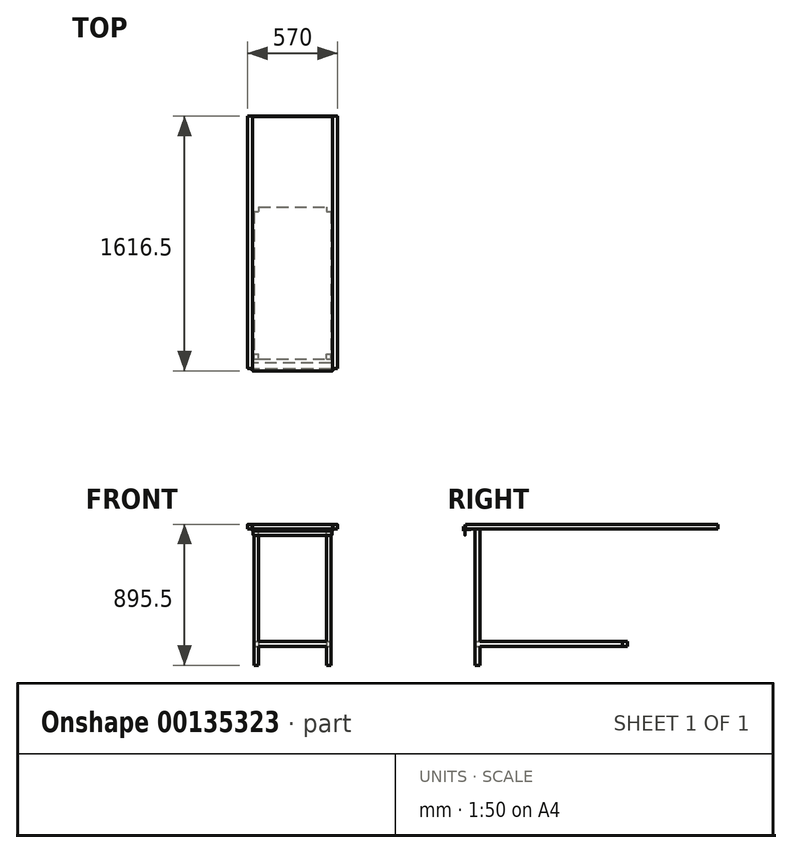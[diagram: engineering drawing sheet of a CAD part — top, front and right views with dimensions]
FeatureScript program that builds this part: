
annotation { "Feature Type Name" : "Feature", "Feature Type Description" : "" }
export const myFeature = defineFeature(function(context is Context, id is Id, definition is map)
    precondition{}
    {
        {
            var Q0;
            Q0=qCreatedBy(makeId("Front.planeOp"),FACE);
            var sketch = newSketch(context, id + "F0", { "sketchPlane" : qUnion([Q0])});
            skLineSegment(sketch, "E0", {"start": v(-285, 0) * mm, "end": v(-285, 28.5) * mm});
            skLineSegment(sketch, "E1", {"start": v(-283.5, 30) * mm, "end": v(-256.5, 30) * mm});
            skLineSegment(sketch, "E2", {"start": v(-255, 28.5) * mm, "end": v(-255, 3) * mm});
            skLineSegment(sketch, "E3", {"start": v(-253.5, 1.5) * mm, "end": v(253.5, 1.5) * mm});
            skLineSegment(sketch, "E4", {"start": v(255, 3) * mm, "end": v(255, 28.5) * mm});
            skLineSegment(sketch, "E5", {"start": v(256.5, 30) * mm, "end": v(283.5, 30) * mm});
            skLineSegment(sketch, "E6", {"start": v(285, 28.5) * mm, "end": v(285, 0) * mm});
            skPoint(sketch, "E7.visualSharp", {"position": v(-285, 30) * mm});
            skArc(sketch, "E7.filletArc", {"start": v(-283.5, 30) * mm, "mid": v(-284.56, 29.56) * mm, "end": v(-285, 28.5) * mm});
            skPoint(sketch, "E8.visualSharp", {"position": v(-255, 30) * mm});
            skArc(sketch, "E8.filletArc", {"start": v(-255, 28.5) * mm, "mid": v(-255.44, 29.56) * mm, "end": v(-256.5, 30) * mm});
            skPoint(sketch, "E9.visualSharp", {"position": v(-255, 1.5) * mm});
            skArc(sketch, "E9.filletArc", {"start": v(-255, 3) * mm, "mid": v(-254.56, 1.94) * mm, "end": v(-253.5, 1.5) * mm});
            skPoint(sketch, "E10.visualSharp", {"position": v(255, 1.5) * mm});
            skArc(sketch, "E10.filletArc", {"start": v(253.5, 1.5) * mm, "mid": v(254.56, 1.94) * mm, "end": v(255, 3) * mm});
            skPoint(sketch, "E11.visualSharp", {"position": v(255, 30) * mm});
            skArc(sketch, "E11.filletArc", {"start": v(256.5, 30) * mm, "mid": v(255.44, 29.56) * mm, "end": v(255, 28.5) * mm});
            skPoint(sketch, "E12.visualSharp", {"position": v(285, 30) * mm});
            skArc(sketch, "E12.filletArc", {"start": v(285, 28.5) * mm, "mid": v(284.56, 29.56) * mm, "end": v(283.5, 30) * mm});
            skLineSegment(sketch, "E13.0", {"start": v(283.5, 28.5) * mm, "end": v(283.5, 0) * mm});
            skLineSegment(sketch, "E13.1", {"start": v(256.5, 28.5) * mm, "end": v(283.5, 28.5) * mm});
            skLineSegment(sketch, "E13.2", {"start": v(256.5, 3) * mm, "end": v(256.5, 28.5) * mm});
            skArc(sketch, "E13.3", {"start": v(253.5, 0) * mm, "mid": v(255.62, 0.88) * mm, "end": v(256.5, 3) * mm});
            skLineSegment(sketch, "E13.4", {"start": v(-253.5, 0) * mm, "end": v(253.5, 0) * mm});
            skLineSegment(sketch, "E13.5", {"start": v(-283.5, 0) * mm, "end": v(-283.5, 28.5) * mm});
            skLineSegment(sketch, "E13.6", {"start": v(-283.5, 28.5) * mm, "end": v(-256.5, 28.5) * mm});
            skLineSegment(sketch, "E13.7", {"start": v(-256.5, 28.5) * mm, "end": v(-256.5, 3) * mm});
            skArc(sketch, "E13.8", {"start": v(-256.5, 3) * mm, "mid": v(-255.62, 0.88) * mm, "end": v(-253.5, 0) * mm});
            skLineSegment(sketch, "E14", {"start": v(-285, 0) * mm, "end": v(-283.5, 0) * mm});
            skLineSegment(sketch, "E15", {"start": v(283.5, 0) * mm, "end": v(285, 0) * mm});
            skSolve(sketch);
        }
        {
            var Q0;
            Q0 = qSketchRegion(id + "F0", true);
            extrude(context, id + "F1", {"entities" : qUnion([Q0]), "depth" : 1600 * mm, "offsetDistance" : 25 * mm});
        }
        {
            var Q0;
            Q0=makeQuery(id+"F1.opExtrude","CAP_FACE",FACE,{"disambiguationData":[OSD([sQuery(id+"F0.wireOp",EDGE,"E0"),sQuery(id+"F0.wireOp",EDGE,"E1"),sQuery(id+"F0.wireOp",EDGE,"E2"),sQuery(id+"F0.wireOp",EDGE,"E3"),sQuery(id+"F0.wireOp",EDGE,"E4"),sQuery(id+"F0.wireOp",EDGE,"E5"),sQuery(id+"F0.wireOp",EDGE,"E6"),sQuery(id+"F0.wireOp",EDGE,"E7.filletArc"),sQuery(id+"F0.wireOp",EDGE,"E8.filletArc"),sQuery(id+"F0.wireOp",EDGE,"E9.filletArc"),sQuery(id+"F0.wireOp",EDGE,"E10.filletArc"),sQuery(id+"F0.wireOp",EDGE,"E11.filletArc"),sQuery(id+"F0.wireOp",EDGE,"E12.filletArc"),sQuery(id+"F0.wireOp",EDGE,"E13.0"),sQuery(id+"F0.wireOp",EDGE,"E13.1"),sQuery(id+"F0.wireOp",EDGE,"E13.2"),sQuery(id+"F0.wireOp",EDGE,"E13.3"),sQuery(id+"F0.wireOp",EDGE,"E13.4"),sQuery(id+"F0.wireOp",EDGE,"E13.5"),sQuery(id+"F0.wireOp",EDGE,"E13.6"),sQuery(id+"F0.wireOp",EDGE,"E13.7"),sQuery(id+"F0.wireOp",EDGE,"E13.8"),sQuery(id+"F0.wireOp",EDGE,"E14"),sQuery(id+"F0.wireOp",EDGE,"E15")])],"isStart":true});
            var sketch = newSketch(context, id + "F2", { "sketchPlane" : qUnion([Q0])});
            skLineSegment(sketch, "E16.0", {"start": v(-285, 28.5) * mm, "end": v(-285, 0) * mm});
            skArc(sketch, "E16.3", {"start": v(283.5, 30) * mm, "mid": v(284.56, 29.56) * mm, "end": v(285, 28.5) * mm});
            skLineSegment(sketch, "E16.4", {"start": v(285, 0) * mm, "end": v(285, 28.5) * mm});
            skArc(sketch, "E16.10", {"start": v(-285, 28.5) * mm, "mid": v(-284.56, 29.56) * mm, "end": v(-283.5, 30) * mm});
            skLineSegment(sketch, "E17", {"start": v(285, 0) * mm, "end": v(-285, 0) * mm});
            skLineSegment(sketch, "E18", {"start": v(-283.5, 30) * mm, "end": v(283.5, 30) * mm});
            skSolve(sketch);
        }
        {
            var Q0;
            Q0 = qSketchRegion(id + "F2", true);
            extrude(context, id + "F3", {"entities" : qUnion([Q0]), "operationType" : NewBodyOperationType.ADD, "depth" : 1.5 * mm});
        }
        {
            var Q0;
            Q0=makeQuery(id+"F1.opExtrude","CAP_FACE",FACE,{"disambiguationData":[OSD([sQuery(id+"F0.wireOp",EDGE,"E0"),sQuery(id+"F0.wireOp",EDGE,"E1"),sQuery(id+"F0.wireOp",EDGE,"E2"),sQuery(id+"F0.wireOp",EDGE,"E3"),sQuery(id+"F0.wireOp",EDGE,"E4"),sQuery(id+"F0.wireOp",EDGE,"E5"),sQuery(id+"F0.wireOp",EDGE,"E6"),sQuery(id+"F0.wireOp",EDGE,"E7.filletArc"),sQuery(id+"F0.wireOp",EDGE,"E8.filletArc"),sQuery(id+"F0.wireOp",EDGE,"E9.filletArc"),sQuery(id+"F0.wireOp",EDGE,"E10.filletArc"),sQuery(id+"F0.wireOp",EDGE,"E11.filletArc"),sQuery(id+"F0.wireOp",EDGE,"E12.filletArc"),sQuery(id+"F0.wireOp",EDGE,"E13.0"),sQuery(id+"F0.wireOp",EDGE,"E13.1"),sQuery(id+"F0.wireOp",EDGE,"E13.2"),sQuery(id+"F0.wireOp",EDGE,"E13.3"),sQuery(id+"F0.wireOp",EDGE,"E13.4"),sQuery(id+"F0.wireOp",EDGE,"E13.5"),sQuery(id+"F0.wireOp",EDGE,"E13.6"),sQuery(id+"F0.wireOp",EDGE,"E13.7"),sQuery(id+"F0.wireOp",EDGE,"E13.8"),sQuery(id+"F0.wireOp",EDGE,"E14"),sQuery(id+"F0.wireOp",EDGE,"E15")])],"isStart":false});
            var sketch = newSketch(context, id + "F4", { "sketchPlane" : qUnion([Q0])});
            skLineSegment(sketch, "E19.0", {"start": v(256.5, 3) * mm, "end": v(256.5, 15) * mm});
            skLineSegment(sketch, "E19.1", {"start": v(-256.5, 15) * mm, "end": v(-256.5, 3) * mm});
            skArc(sketch, "E19.2", {"start": v(-256.5, 3) * mm, "mid": v(-255.62, 0.88) * mm, "end": v(-253.5, 0) * mm});
            skLineSegment(sketch, "E19.3", {"start": v(-253.5, 0) * mm, "end": v(253.5, 0) * mm});
            skArc(sketch, "E19.4", {"start": v(253.5, 0) * mm, "mid": v(255.62, 0.88) * mm, "end": v(256.5, 3) * mm});
            skLineSegment(sketch, "E20.0", {"start": v(255, 3) * mm, "end": v(255, 15) * mm});
            skLineSegment(sketch, "E20.1", {"start": v(-255, 15) * mm, "end": v(-255, 3) * mm});
            skArc(sketch, "E20.2", {"start": v(-255, 3) * mm, "mid": v(-254.56, 1.94) * mm, "end": v(-253.5, 1.5) * mm});
            skLineSegment(sketch, "E20.3", {"start": v(-253.5, 1.5) * mm, "end": v(253.5, 1.5) * mm});
            skArc(sketch, "E20.4", {"start": v(253.5, 1.5) * mm, "mid": v(254.56, 1.94) * mm, "end": v(255, 3) * mm});
            skLineSegment(sketch, "E21", {"start": v(-256.5, 15) * mm, "end": v(-255, 15) * mm});
            skLineSegment(sketch, "E22", {"start": v(255, 15) * mm, "end": v(256.5, 15) * mm});
            skSolve(sketch);
        }
        {
            var Q0;
            Q0 = qSketchRegion(id + "F4", true);
            extrude(context, id + "F5", {"entities" : qUnion([Q0]), "operationType" : NewBodyOperationType.ADD, "depth" : 13.5 * mm});
        }
        {
            var Q0;
            Q0=makeQuery(id+"F5.opExtrude","CAP_FACE",FACE,{"disambiguationData":[OSD([sQuery(id+"F4.wireOp",EDGE,"E19.0"),sQuery(id+"F4.wireOp",EDGE,"E19.1"),sQuery(id+"F4.wireOp",EDGE,"E19.2"),sQuery(id+"F4.wireOp",EDGE,"E19.3"),sQuery(id+"F4.wireOp",EDGE,"E19.4"),sQuery(id+"F4.wireOp",EDGE,"E20.0"),sQuery(id+"F4.wireOp",EDGE,"E20.1"),sQuery(id+"F4.wireOp",EDGE,"E20.2"),sQuery(id+"F4.wireOp",EDGE,"E20.3"),sQuery(id+"F4.wireOp",EDGE,"E20.4"),sQuery(id+"F4.wireOp",EDGE,"E21"),sQuery(id+"F4.wireOp",EDGE,"E22")])],"isStart":false});
            var sketch = newSketch(context, id + "F6", { "sketchPlane" : qUnion([Q0])});
            skLineSegment(sketch, "E23.bottom", {"start": v(-253.5, 1.5) * mm, "end": v(253.5, 1.5) * mm});
            skLineSegment(sketch, "E23.top", {"start": v(-253.5, 0) * mm, "end": v(253.5, 0) * mm});
            skLineSegment(sketch, "E23.left", {"start": v(-253.5, 1.5) * mm, "end": v(-253.5, 0) * mm});
            skLineSegment(sketch, "E23.right", {"start": v(253.5, 1.5) * mm, "end": v(253.5, 0) * mm});
            skSolve(sketch);
        }
        {
            var Q0;
            Q0 = qSketchRegion(id + "F6", true);
            var Q1;
            Q1=sQuery(id+"F6.wireOp",EDGE,"E23.top");
            revolve(context, id + "F7", {"operationType" : NewBodyOperationType.ADD, "entities" : qUnion([Q0]), "axis" : qUnion([Q1]), "revolveType" : RevolveType.ONE_DIRECTION, "angle" : 90 * degree});
        }
        {
            var Q0;
            Q0=makeQuery(id+"F7.boolean.opBoolean","MERGE",FACE,{"derivedFrom":[makeQuery(id+"F5.boolean.opBoolean","MERGE",FACE,{"derivedFrom":[makeQuery(id+"F3.boolean.opBoolean","MERGE",FACE,{"derivedFrom":[makeQuery(id+"F1.opExtrude","SWEPT_FACE",FACE,{"disambiguationData":[OSD([sQuery(id+"F0.wireOp",EDGE,"E13.4")])]}),makeQuery(id+"F1.opExtrude","SWEPT_FACE",FACE,{"disambiguationData":[OSD([sQuery(id+"F0.wireOp",EDGE,"E14")])]}),makeQuery(id+"F1.opExtrude","SWEPT_FACE",FACE,{"disambiguationData":[OSD([sQuery(id+"F0.wireOp",EDGE,"E15")])]}),makeQuery(id+"F3.opExtrude","SWEPT_FACE",FACE,{"disambiguationData":[OSD([sQuery(id+"F2.wireOp",EDGE,"E17")])]})]}),makeQuery(id+"F5.opExtrude","SWEPT_FACE",FACE,{"disambiguationData":[OSD([sQuery(id+"F4.wireOp",EDGE,"E19.3")])]})]}),makeQuery(id+"F7.opRevolve","CAP_FACE",FACE,{"disambiguationData":[OSD([sQuery(id+"F6.wireOp",EDGE,"E23.bottom"),sQuery(id+"F6.wireOp",EDGE,"E23.top"),sQuery(id+"F6.wireOp",EDGE,"E23.left"),sQuery(id+"F6.wireOp",EDGE,"E23.right")])],"isStart":false})]});
            var sketch = newSketch(context, id + "F8", { "sketchPlane" : qUnion([Q0])});
            skLineSegment(sketch, "E24.bottom", {"start": v(-253.5, 1615) * mm, "end": v(253.5, 1615) * mm});
            skLineSegment(sketch, "E24.top", {"start": v(-253.5, 1613.5) * mm, "end": v(253.5, 1613.5) * mm});
            skLineSegment(sketch, "E24.left", {"start": v(-253.5, 1615) * mm, "end": v(-253.5, 1613.5) * mm});
            skLineSegment(sketch, "E24.right", {"start": v(253.5, 1615) * mm, "end": v(253.5, 1613.5) * mm});
            skSolve(sketch);
        }
        {
            var Q0;
            Q0 = qSketchRegion(id + "F8", true);
            extrude(context, id + "F9", {"entities" : qUnion([Q0]), "operationType" : NewBodyOperationType.ADD, "depth" : 13.5 * mm});
        }
        {
            var Q0;
            Q0=makeQuery(id+"F1.opExtrude","SWEPT_FACE",FACE,{"disambiguationData":[OSD([sQuery(id+"F0.wireOp",EDGE,"E13.0")])]});
            var sketch = newSketch(context, id + "F10", { "sketchPlane" : qUnion([Q0])});
            skLineSegment(sketch, "E25.bottom", {"start": v(1600, 28.5) * mm, "end": v(1598.5, 28.5) * mm});
            skLineSegment(sketch, "E25.top", {"start": v(1600, 0) * mm, "end": v(1598.5, 0) * mm});
            skLineSegment(sketch, "E25.left", {"start": v(1600, 28.5) * mm, "end": v(1600, 0) * mm});
            skLineSegment(sketch, "E25.right", {"start": v(1598.5, 28.5) * mm, "end": v(1598.5, 0) * mm});
            skSolve(sketch);
        }
        {
            var Q0;
            Q0 = qSketchRegion(id + "F10", true);
            extrude(context, id + "F11", {"entities" : qUnion([Q0]), "operationType" : NewBodyOperationType.ADD, "endBound" : BoundingType.UP_TO_NEXT, "depth" : 25 * mm});
        }
        {
            var Q0;
            Q0=makeQuery(id+"F1.opExtrude","SWEPT_FACE",FACE,{"disambiguationData":[OSD([sQuery(id+"F0.wireOp",EDGE,"E13.5")])]});
            var sketch = newSketch(context, id + "F12", { "sketchPlane" : qUnion([Q0])});
            skLineSegment(sketch, "E26.bottom", {"start": v(-1600, 28.5) * mm, "end": v(-1598.5, 28.5) * mm});
            skLineSegment(sketch, "E26.top", {"start": v(-1600, 0) * mm, "end": v(-1598.5, 0) * mm});
            skLineSegment(sketch, "E26.left", {"start": v(-1600, 28.5) * mm, "end": v(-1600, 0) * mm});
            skLineSegment(sketch, "E26.right", {"start": v(-1598.5, 28.5) * mm, "end": v(-1598.5, 0) * mm});
            skSolve(sketch);
        }
        {
            var Q0;
            Q0 = qSketchRegion(id + "F12", true);
            extrude(context, id + "F13", {"entities" : qUnion([Q0]), "operationType" : NewBodyOperationType.ADD, "endBound" : BoundingType.UP_TO_NEXT, "depth" : 25 * mm});
        }
        {
            var Q0;
            Q0=makeQuery(id+"F13.boolean.opBoolean","MERGE",FACE,{"derivedFrom":[makeQuery(id+"F11.boolean.opBoolean","MERGE",FACE,{"derivedFrom":[makeQuery(id+"F7.boolean.opBoolean","MERGE",FACE,{"derivedFrom":[makeQuery(id+"F5.boolean.opBoolean","MERGE",FACE,{"derivedFrom":[makeQuery(id+"F3.boolean.opBoolean","MERGE",FACE,{"derivedFrom":[makeQuery(id+"F1.opExtrude","SWEPT_FACE",FACE,{"disambiguationData":[OSD([sQuery(id+"F0.wireOp",EDGE,"E13.4")])]}),makeQuery(id+"F1.opExtrude","SWEPT_FACE",FACE,{"disambiguationData":[OSD([sQuery(id+"F0.wireOp",EDGE,"E14")])]}),makeQuery(id+"F1.opExtrude","SWEPT_FACE",FACE,{"disambiguationData":[OSD([sQuery(id+"F0.wireOp",EDGE,"E15")])]}),makeQuery(id+"F3.opExtrude","SWEPT_FACE",FACE,{"disambiguationData":[OSD([sQuery(id+"F2.wireOp",EDGE,"E17")])]})]}),makeQuery(id+"F5.opExtrude","SWEPT_FACE",FACE,{"disambiguationData":[OSD([sQuery(id+"F4.wireOp",EDGE,"E19.3")])]})]}),makeQuery(id+"F7.opRevolve","CAP_FACE",FACE,{"disambiguationData":[OSD([sQuery(id+"F6.wireOp",EDGE,"E23.bottom"),sQuery(id+"F6.wireOp",EDGE,"E23.top"),sQuery(id+"F6.wireOp",EDGE,"E23.left"),sQuery(id+"F6.wireOp",EDGE,"E23.right")])],"isStart":false})]}),makeQuery(id+"F11.opExtrude","SWEPT_FACE",FACE,{"disambiguationData":[OSD([sQuery(id+"F10.wireOp",EDGE,"E25.top")])]})]}),makeQuery(id+"F13.opExtrude","SWEPT_FACE",FACE,{"disambiguationData":[OSD([sQuery(id+"F12.wireOp",EDGE,"E26.top")])]})]});
            var sketch = newSketch(context, id + "F14", { "sketchPlane" : qUnion([Q0])});
            skLineSegment(sketch, "E27.bottom", {"start": v(250, 1605.5) * mm, "end": v(-250, 1605.5) * mm});
            skLineSegment(sketch, "E27.top", {"start": v(245, 1565.5) * mm, "end": v(-245, 1565.5) * mm});
            skLineSegment(sketch, "E27.left", {"start": v(250, 1605.5) * mm, "end": v(250, 1570.5) * mm});
            skLineSegment(sketch, "E27.right", {"start": v(-250, 1605.5) * mm, "end": v(-250, 1570.5) * mm});
            skPoint(sketch, "E28.visualSharp", {"position": v(250, 1565.5) * mm});
            skArc(sketch, "E28.filletArc", {"start": v(245, 1565.5) * mm, "mid": v(248.54, 1566.96) * mm, "end": v(250, 1570.5) * mm});
            skPoint(sketch, "E29.visualSharp", {"position": v(-250, 1565.5) * mm});
            skArc(sketch, "E29.filletArc", {"start": v(-250, 1570.5) * mm, "mid": v(-248.54, 1566.96) * mm, "end": v(-245, 1565.5) * mm});
            skSolve(sketch);
        }
        {
            var Q0;
            Q0 = qSketchRegion(id + "F14", true);
            extrude(context, id + "F15", {"entities" : qUnion([Q0]), "operationType" : NewBodyOperationType.ADD, "depth" : 1.5 * mm});
        }
        {
            var Q0;
            Q0=makeQuery(id+"F15.opExtrude","CAP_FACE",FACE,{"disambiguationData":[OSD([sQuery(id+"F14.wireOp",EDGE,"E27.bottom"),sQuery(id+"F14.wireOp",EDGE,"E27.top"),sQuery(id+"F14.wireOp",EDGE,"E27.left"),sQuery(id+"F14.wireOp",EDGE,"E27.right"),sQuery(id+"F14.wireOp",EDGE,"E28.filletArc"),sQuery(id+"F14.wireOp",EDGE,"E29.filletArc")])],"isStart":false});
            var sketch = newSketch(context, id + "F16", { "sketchPlane" : qUnion([Q0])});
            skLineSegment(sketch, "E30.bottom", {"start": v(250, 1605.5) * mm, "end": v(-250, 1605.5) * mm});
            skLineSegment(sketch, "E30.top", {"start": v(250, 1604) * mm, "end": v(-250, 1604) * mm});
            skLineSegment(sketch, "E30.left", {"start": v(250, 1605.5) * mm, "end": v(250, 1604) * mm});
            skLineSegment(sketch, "E30.right", {"start": v(-250, 1605.5) * mm, "end": v(-250, 1604) * mm});
            skSolve(sketch);
        }
        {
            var Q0;
            Q0 = qSketchRegion(id + "F16", true);
            extrude(context, id + "F17", {"entities" : qUnion([Q0]), "operationType" : NewBodyOperationType.ADD, "depth" : 38.5 * mm});
        }
        {
            var Q0;
            Q0=makeQuery(id+"F17.opExtrude","CAP_EDGE",EDGE,{"disambiguationData":[OSD([sQuery(id+"F16.wireOp",EDGE,"E30.right")])],"isStart":false});
            var Q1;
            Q1=makeQuery(id+"F17.opExtrude","CAP_EDGE",EDGE,{"disambiguationData":[OSD([sQuery(id+"F16.wireOp",EDGE,"E30.left")])],"isStart":false});
            fillet(context, id + "F18", {"entities" : qUnion([Q0, Q1]), "radius" : 5 * mm, "tangentPropagation" : true, "allowEdgeOverflow" : false});
        }
        {
            var Q0;
            Q0=makeQuery(id+"F13.boolean.opBoolean","MERGE",FACE,{"derivedFrom":[makeQuery(id+"F11.boolean.opBoolean","MERGE",FACE,{"derivedFrom":[makeQuery(id+"F7.boolean.opBoolean","MERGE",FACE,{"derivedFrom":[makeQuery(id+"F5.boolean.opBoolean","MERGE",FACE,{"derivedFrom":[makeQuery(id+"F3.boolean.opBoolean","MERGE",FACE,{"derivedFrom":[makeQuery(id+"F1.opExtrude","SWEPT_FACE",FACE,{"disambiguationData":[OSD([sQuery(id+"F0.wireOp",EDGE,"E13.4")])]}),makeQuery(id+"F1.opExtrude","SWEPT_FACE",FACE,{"disambiguationData":[OSD([sQuery(id+"F0.wireOp",EDGE,"E14")])]}),makeQuery(id+"F1.opExtrude","SWEPT_FACE",FACE,{"disambiguationData":[OSD([sQuery(id+"F0.wireOp",EDGE,"E15")])]}),makeQuery(id+"F3.opExtrude","SWEPT_FACE",FACE,{"disambiguationData":[OSD([sQuery(id+"F2.wireOp",EDGE,"E17")])]})]}),makeQuery(id+"F5.opExtrude","SWEPT_FACE",FACE,{"disambiguationData":[OSD([sQuery(id+"F4.wireOp",EDGE,"E19.3")])]})]}),makeQuery(id+"F7.opRevolve","CAP_FACE",FACE,{"disambiguationData":[OSD([sQuery(id+"F6.wireOp",EDGE,"E23.bottom"),sQuery(id+"F6.wireOp",EDGE,"E23.top"),sQuery(id+"F6.wireOp",EDGE,"E23.left"),sQuery(id+"F6.wireOp",EDGE,"E23.right")])],"isStart":false})]}),makeQuery(id+"F11.opExtrude","SWEPT_FACE",FACE,{"disambiguationData":[OSD([sQuery(id+"F10.wireOp",EDGE,"E25.top")])]})]}),makeQuery(id+"F13.opExtrude","SWEPT_FACE",FACE,{"disambiguationData":[OSD([sQuery(id+"F12.wireOp",EDGE,"E26.top")])]})]});
            var sketch = newSketch(context, id + "F19", { "sketchPlane" : qUnion([Q0])});
            skLineSegment(sketch, "E31.bottom", {"start": v(-245, 1540) * mm, "end": v(-215, 1540) * mm});
            skLineSegment(sketch, "E31.top", {"start": v(-245, 1510) * mm, "end": v(-215, 1510) * mm});
            skLineSegment(sketch, "E31.left", {"start": v(-245, 1540) * mm, "end": v(-245, 1510) * mm});
            skLineSegment(sketch, "E31.right", {"start": v(-215, 1540) * mm, "end": v(-215, 1510) * mm});
            skPoint(sketch, "E31.middle", {"position": v(-230, 1525) * mm});
            skLineSegment(sketch, "E32.bottom", {"start": v(215, 1540) * mm, "end": v(245, 1540) * mm});
            skLineSegment(sketch, "E32.top", {"start": v(215, 1510) * mm, "end": v(245, 1510) * mm});
            skLineSegment(sketch, "E32.left", {"start": v(215, 1540) * mm, "end": v(215, 1510) * mm});
            skLineSegment(sketch, "E32.right", {"start": v(245, 1540) * mm, "end": v(245, 1510) * mm});
            skPoint(sketch, "E32.middle", {"position": v(230, 1525) * mm});
            skSolve(sketch);
        }
        {
            var Q0;
            Q0 = qSketchRegion(id + "F19", true);
            extrude(context, id + "F20", {"entities" : qUnion([Q0]), "operationType" : NewBodyOperationType.ADD, "depth" : 865.5 * mm, "offsetDistance" : 25 * mm});
        }
        {
            var Q0;
            Q0=makeQuery(id+"F20.opExtrude","SWEPT_FACE",FACE,{"disambiguationData":[OSD([sQuery(id+"F19.wireOp",EDGE,"E31.bottom")])]});
            var sketch = newSketch(context, id + "F21", { "sketchPlane" : qUnion([Q0])});
            skLineSegment(sketch, "E33.bottom", {"start": v(-245, -715.5) * mm, "end": v(245, -715.5) * mm});
            skLineSegment(sketch, "E33.top", {"start": v(-245, -745.5) * mm, "end": v(245, -745.5) * mm});
            skLineSegment(sketch, "E33.left", {"start": v(-245, -715.5) * mm, "end": v(-245, -745.5) * mm});
            skLineSegment(sketch, "E33.right", {"start": v(245, -715.5) * mm, "end": v(245, -745.5) * mm});
            skSolve(sketch);
        }
        {
            var Q0;
            Q0 = qSketchRegion(id + "F21", true);
            extrude(context, id + "F22", {"entities" : qUnion([Q0]), "operationType" : NewBodyOperationType.ADD, "oppositeDirection" : true, "depth" : 936.5 * mm, "offsetDistance" : 25 * mm});
        }
        {
            var Q0;
            Q0=makeQuery(id+"F22.opExtrude","CAP_FACE",FACE,{"disambiguationData":[OSD([sQuery(id+"F21.wireOp",EDGE,"E33.bottom"),sQuery(id+"F21.wireOp",EDGE,"E33.top"),sQuery(id+"F21.wireOp",EDGE,"E33.left"),sQuery(id+"F21.wireOp",EDGE,"E33.right")])],"isStart":false});
            var sketch = newSketch(context, id + "F23", { "sketchPlane" : qUnion([Q0])});
            skLineSegment(sketch, "E34.bottom", {"start": v(-215, -715.5) * mm, "end": v(215, -715.5) * mm});
            skLineSegment(sketch, "E34.top", {"start": v(-215, -745.5) * mm, "end": v(215, -745.5) * mm});
            skLineSegment(sketch, "E34.left", {"start": v(-215, -715.5) * mm, "end": v(-215, -745.5) * mm});
            skLineSegment(sketch, "E34.right", {"start": v(215, -715.5) * mm, "end": v(215, -745.5) * mm});
            skSolve(sketch);
        }
        {
            var Q0;
            Q0 = qSketchRegion(id + "F23", true);
            extrude(context, id + "F24", {"entities" : qUnion([Q0]), "operationType" : NewBodyOperationType.ADD, "depth" : 30 * mm, "offsetDistance" : 25 * mm});
        }
    });
